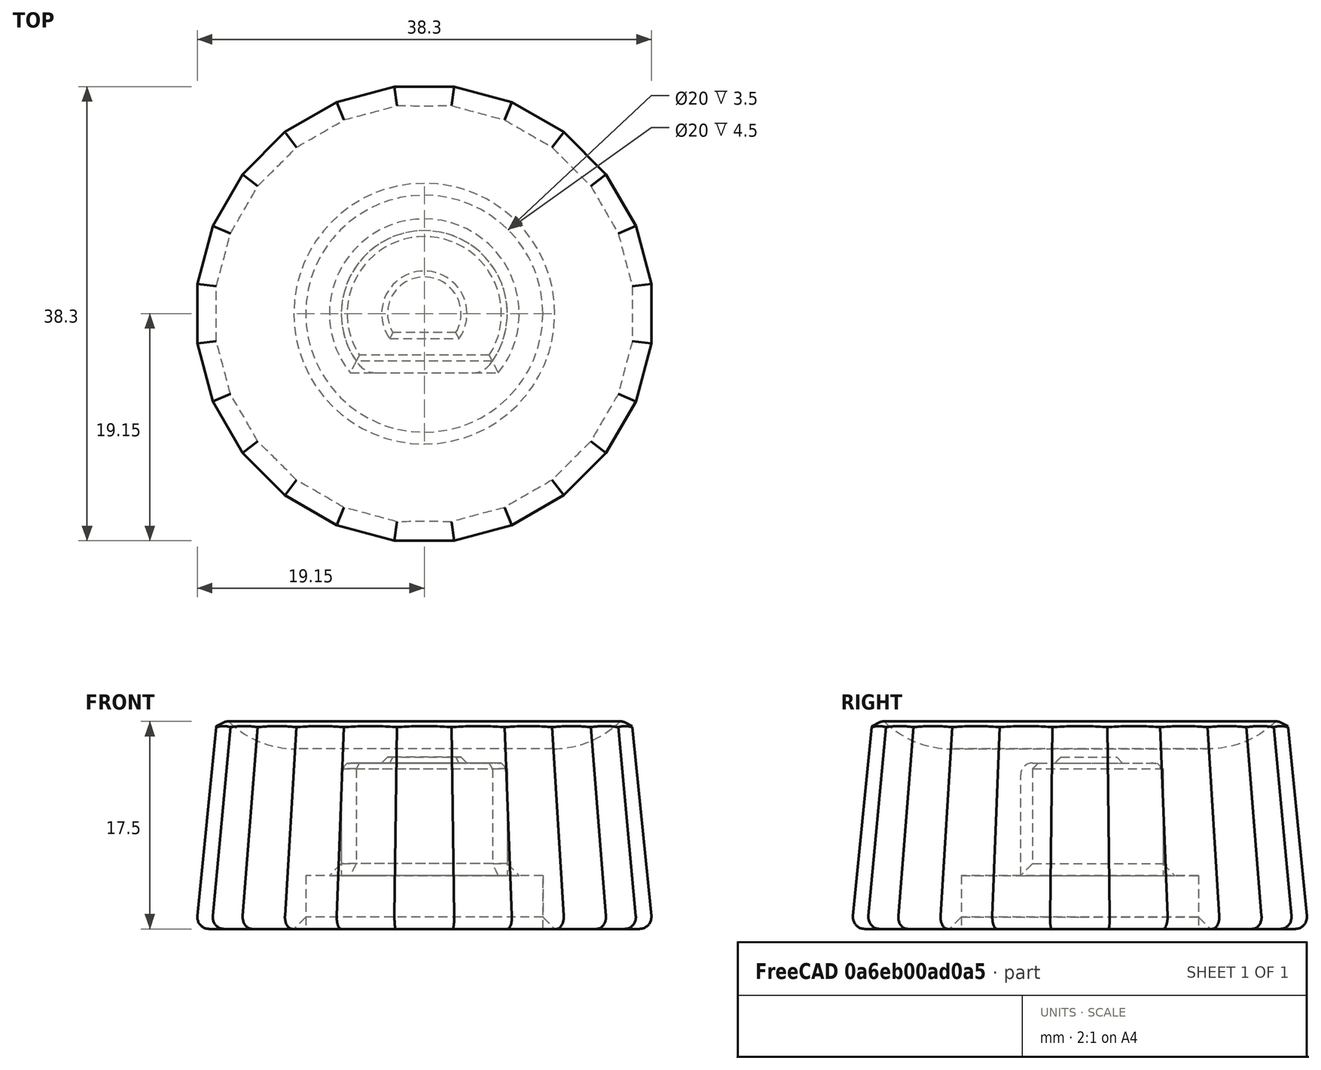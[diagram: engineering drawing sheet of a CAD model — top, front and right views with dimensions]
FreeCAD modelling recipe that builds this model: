
FCSTD DOCUMENT  (FreeCAD 1.0R39319 (Git))
Label: KNOB-TEK2
License: All rights reserved
LicenseURL: https://en.wikipedia.org/wiki/All_rights_reserved
objects: TechDraw::DrawViewDimension×14, Sketcher::SketchObject×7, TechDraw::DrawViewPart×5, TechDraw::DrawHatch×5, TechDraw::DrawViewBalloon×4, TechDraw::DrawViewAnnotation×2, PartDesign::Pocket×2, PartDesign::CoordinateSystem×2, Part::Feature×1, PartDesign::Plane×1, PartDesign::Pad×1, PartDesign::Boolean×1, TechDraw::DrawSVGTemplate×1, PartDesign::Fillet×1, PartDesign::Body×1, TechDraw::DrawComplexSection×1, TechDraw::DrawViewDimExtent×1, TechDraw::DrawPage×1
note: 58 computed .brp shape members not serialized (recipe doc carries the construction recipe); baked Part::Feature solids carry a one-line shape summary decoded from their .brp

FEATURE [Part::Feature] Part__Feature  label="alu_potmeter_002_04"
  shape: bbox 38.3 x 38.3 x 17.53 mm, 68 faces (baked)
FEATURE [PartDesign::Plane] DatumPlane
  AttachmentOffset = pos=(0,0,4.5) rot=(0,0,1;0rad)
  AttachmentSupport = -> [XY_Plane]
  Length = 60
  MapMode = 5
  Placement = pos=(0,0,4.5) rot=(0,0,1;0rad)
  ResizeMode = 0
  Width = 60
FEATURE [Sketcher::SketchObject] Sketch
  ArcFitTolerance = 0
  AttachmentSupport = -> [XY_Plane]
  FullyConstrained = true
  MakeInternals = false
  MapMode = 2
  sketch-geometry (1):
    g0: Circle CenterX=0 CenterY=0 CenterZ=0 NormalX=0 NormalY=0 NormalZ=1 AngleXU=0 Radius=15
  constraints (2):
    c: Coincident(g0,g-1)
    c: Diameter(g0) = 30
FEATURE [PartDesign::Pad] Pad
  Direction = (0,0,1)
  Length = 15
  Length2 = 10
  Profile = -> Sketch
  ReferenceAxis = -> Sketch [N_Axis]
  Refine = true
  Suppressed = false
  Type = 0
FEATURE [Sketcher::SketchObject] Sketch001
  ArcFitTolerance = 0
  AttachmentSupport = -> [DatumPlane]
  FullyConstrained = true
  MakeInternals = false
  MapMode = 5
  Placement = pos=(0,0,4.5) rot=(0,0,1;0rad)
  sketch-geometry (7):
    g0: ArcOfCircle CenterX=0 CenterY=0 CenterZ=0 NormalX=0 NormalY=0 NormalZ=1 AngleXU=0 Radius=7 StartAngle=5.63968 EndAngle=10.0683
    g1: LineSegment StartX=-4 StartY=-5 StartZ=0 EndX=4 EndY=-5 EndZ=0
    g2: Circle [constr] CenterX=0 CenterY=0 CenterZ=0 NormalX=0 NormalY=0 NormalZ=1 AngleXU=0 Radius=4.25
    g3: LineSegment [constr] StartX=0 StartY=-4.25 StartZ=0 EndX=0 EndY=-5 EndZ=0
    g4: ArcOfCircle CenterX=-4 CenterY=-3 CenterZ=0 NormalX=0 NormalY=0 NormalZ=1 AngleXU=0 Radius=2 StartAngle=3.78509 EndAngle=4.71239
    g5: ArcOfCircle CenterX=4 CenterY=-3 CenterZ=0 NormalX=0 NormalY=0 NormalZ=1 AngleXU=0 Radius=2 StartAngle=4.71239 EndAngle=5.63968
    g6: GeomPoint [constr] X=0 Y=7 Z=0
  constraints (20):
    c: Coincident(g0,g-1)
    c: Diameter(g0) = 14
    c: Horizontal(g1)
    c: Coincident(g2,g0)
    c: Diameter(g2) = 8.5
    c: PointOnObject(g3,g2)
    c: PointOnObject(g3,g1)
    c: Vertical(g3)
    c: PointOnObject(g3,g-2)
    c: DistanceY(g3,g3) = 0.75
    c: Tangent(g1,g4) = -1.5708
    c: Tangent(g0,g4) = -1.5708
    c: Tangent(g1,g5) = -1.5708
    c: Tangent(g0,g5) = -1.5708
    c: Equal(g5,g4)
    c: Diameter(g5) = 4
    c: DistanceY(g3,g0) = 5
    c: PointOnObject(g6,g0)
    c: PointOnObject(g6,g-2)
    c: DistanceY(g3,g6) = 12
FEATURE [PartDesign::Boolean] Boolean
  BaseFeature = -> Pad
  Group = -> [Part__Feature]
  Refine = true
  Suppressed = false
  Type = 0
  UsePlacement = false
FEATURE [TechDraw::DrawSVGTemplate] Template
  EditableTexts = COLOR=Sandblasted, black anodized (RAL code: 9004); CreationDate=2024/08/27; E.G.APPROVED=APPROVED; FC-Scale=2:1; FC-Title=KNOB-TEK2; IntechStudioLtd.=Intech Studio Ltd.; MATERIAL=Aluminum 6061-T6; REV=03; STANDARD=DIN 16742-TG5
  Height = 297
  Orientation = 1
  Template = <userpath>/Documents/grid-hardware/Manufacturing/FreeCAD_technical_drawing_template/A3_LandscapeTD_MODIFIED.svg
  Width = 420
FEATURE [Sketcher::SketchObject] Sketch002
  ArcFitTolerance = 0
  AttachmentSupport = -> [YZ_Plane]
  FullyConstrained = true
  MakeInternals = false
  MapMode = 5
  Placement = pos=(0,0,0) rot=(0.57735,0.57735,0.57735;2.0944rad)
  sketch-geometry (1):
    g0: LineSegment StartX=0 StartY=20 StartZ=0 EndX=0 EndY=-5 EndZ=0
  constraints (4):
    c: PointOnObject(g0,g-2)
    c: PointOnObject(g0,g-2)
    c: DistanceY(g0,g0) = 25
    c: DistanceY(g0,g-1) = 5
FEATURE [TechDraw::DrawViewAnnotation] Annotation
  Font = osifont
  LineSpace = 100
  LockPosition = false
  MaxWidth = -1
  Rotation = 0
  Scale = 2
  ScaleType = 0
  Text = Non-aesthetical side (purple): | No burrs
  TextSize = 5
  TextStyle = 0
  X = 278.355
  Y = 88.8334
FEATURE [Sketcher::SketchObject] Sketch004
  ArcFitTolerance = 0
  AttachmentSupport = -> [XY_Plane]
  FullyConstrained = true
  MakeInternals = false
  MapMode = 5
  sketch-geometry (1):
    g0: Circle CenterX=0 CenterY=0 CenterZ=0 NormalX=0 NormalY=0 NormalZ=1 AngleXU=0 Radius=10
  constraints (2):
    c: Coincident(g0,g-1)
    c: Diameter(g0) = 20
FEATURE [PartDesign::Pocket] Pocket001
  BaseFeature = -> Boolean
  Direction = (0,0,-1)
  Length = 4.5
  Length2 = 5
  Profile = -> Sketch004
  ReferenceAxis = -> Sketch004 [N_Axis]
  Refine = true
  Reversed = true
  Suppressed = false
  Type = 0
FEATURE [PartDesign::Pocket] Pocket
  BaseFeature = -> Pocket001
  Direction = (0,0,-1)
  Length = 9.5
  Length2 = 5
  Profile = -> Sketch001
  ReferenceAxis = -> Sketch001 [N_Axis]
  Refine = true
  Reversed = true
  Suppressed = false
  Type = 0
FEATURE [TechDraw::DrawViewAnnotation] Annotation001
  Font = osifont
  LineSpace = 100
  LockPosition = false
  MaxWidth = -1
  Rotation = 0
  Scale = 2
  ScaleType = 0
  Text = Section A-A
  TextSize = 4
  TextStyle = 0
  X = 199.631
  Y = 206.549
FEATURE [Sketcher::SketchObject] Sketch005
  ArcFitTolerance = 0
  AttachmentSupport = -> [DatumPlane]
  FullyConstrained = true
  MakeInternals = false
  MapMode = 5
  Placement = pos=(0,0,4.5) rot=(0,0,1;0rad)
  sketch-geometry (1):
    g0: Circle CenterX=0 CenterY=0 CenterZ=0 NormalX=0 NormalY=0 NormalZ=1 AngleXU=0 Radius=3.5
  constraints (2):
    c: Coincident(g0,g-1)
    c: Diameter(g0) = 7
FEATURE [PartDesign::Fillet] Fillet
  Base = -> Pocket [Edge136]
  BaseFeature = -> Pocket
  Radius = 1
  SupportTransform = false
  Suppressed = false
  UseAllEdges = false
FEATURE [Sketcher::SketchObject] Sketch006
  ArcFitTolerance = 0
  AttachmentSupport = -> [XY_Plane]
  FullyConstrained = true
  MakeInternals = false
  MapMode = 5
  sketch-geometry (5):
    g0: Circle CenterX=0 CenterY=0 CenterZ=0 NormalX=0 NormalY=0 NormalZ=1 AngleXU=0 Radius=6.975
    g1: Circle CenterX=0 CenterY=0 CenterZ=0 NormalX=0 NormalY=0 NormalZ=1 AngleXU=0 Radius=4.3
    g2: LineSegment StartX=-4.88876 StartY=4.975 StartZ=0 EndX=4.88876 EndY=4.975 EndZ=0
    g3: GeomPoint [constr] X=0 Y=-6.975 Z=0
    g4: GeomPoint [constr] X=0 Y=4.3 Z=0
  constraints (13):
    c: Coincident(g0,g-1)
    c: Coincident(g1,g0)
    c: PointOnObject(g2,g0)
    c: PointOnObject(g2,g0)
    c: Horizontal(g2)
    c: Diameter(g0) = 13.95
    c: Diameter(g1) = 8.6
    c: PointOnObject(g3,g0)
    c: PointOnObject(g3,g-2)
    c: DistanceY(g3,g2) = 11.95
    c: PointOnObject(g4,g1)
    c: DistanceY(g4,g2) = 0.675
    c: PointOnObject(g4,g-2)
FEATURE [Sketcher::SketchObject] Sketch007
  ArcFitTolerance = 0
  AttachmentSupport = -> [XY_Plane]
  FullyConstrained = true
  MakeInternals = false
  MapMode = 5
  sketch-geometry (4):
    g0: Circle CenterX=0 CenterY=0 CenterZ=0 NormalX=0 NormalY=0 NormalZ=1 AngleXU=0 Radius=0.1
    g1: Circle CenterX=0 CenterY=0.1 CenterZ=0 NormalX=0 NormalY=0 NormalZ=1 AngleXU=0 Radius=3.475
    g2: Circle CenterX=0 CenterY=-0.1 CenterZ=0 NormalX=0 NormalY=0 NormalZ=1 AngleXU=0 Radius=2.95
    g3: LineSegment StartX=0 StartY=-3.05 StartZ=0 EndX=0 EndY=-3.375 EndZ=0
  constraints (13):
    c: Coincident(g0,g-1)
    c: Diameter(g0) = 0.2
    c: PointOnObject(g1,g-2)
    c: PointOnObject(g1,g0)
    c: Diameter(g1) = 6.95
    c: PointOnObject(g2,g0)
    c: PointOnObject(g2,g-2)
    c: Diameter(g2) = 5.9
    c: PointOnObject(g3,g2)
    c: PointOnObject(g3,g1)
    c: Vertical(g3)
    c: PointOnObject(g3,g-2)
    c: DistanceY(g3,g3) = 0.325
FEATURE [PartDesign::CoordinateSystem] LCS_1
  AttacherType = Attacher::AttachEngine3D
  AttachmentSupport = -> [Fillet]
  MapMode = 45
  Placement = pos=(5e-16,0.740493,14) rot=(0,0,1;1.5708rad)
FEATURE [PartDesign::CoordinateSystem] LCS_2
  AttacherType = Attacher::AttachEngine3D
  AttachmentSupport = -> [Fillet]
  MapMode = 5
  Placement = pos=(0,0,14) rot=(1,0,0;3.14159rad)
FEATURE [PartDesign::Body] Body  label="KNOB-TEK2"
  AllowCompound = false
  Group = -> [DatumPlane,Sketch,Pad,Boolean,Pocket001,Sketch001,Pocket,Sketch002,Sketch004,Sketch005,Fillet,Sketch006,Sketch007,LCS_1,LCS_2]
  Origin = -> Origin
  Tip = -> Fillet
FEATURE [TechDraw::DrawViewPart] View
  CoarseView = false
  Direction = (-1,0,-3e-06)
  Focus = 100
  HardHidden = false
  IsoCount = 0
  IsoHidden = false
  IsoVisible = true
  LockPosition = false
  Perspective = false
  Rotation = 0
  Scale = 2
  ScaleType = 2
  ScrubCount = 0
  SeamHidden = false
  SeamVisible = true
  SmoothHidden = false
  SmoothVisible = true
  Source = -> [Body]
  X = 71.6241
  XDirection = (0,-1,0)
  Y = 240.603
FEATURE [TechDraw::DrawComplexSection] ComplexSection  label="Section A - A"
  BaseView = -> View
  CoarseView = false
  CutSurfaceDisplay = 3
  CuttingToolWireObject = -> Sketch002
  Direction = (0,1,-1e-16)
  FileGeomPattern = C:/Program Files/FreeCAD 0.21/data/Mod/TechDraw/PAT/FCPAT.pat
  FileHatchPattern = C:/Program Files/FreeCAD 0.21/data/Mod/TechDraw/Patterns/simple.svg
  Focus = 100
  FuseBeforeCut = false
  HardHidden = false
  HatchOffset = (0,0,0)
  HatchRotation = 0
  HatchScale = 1
  IsoCount = 0
  IsoHidden = false
  IsoVisible = true
  LockPosition = false
  NameGeomPattern = Gyémánt bevonatú
  Perspective = false
  ProjectionStrategy = 0
  Rotation = -90
  Scale = 2
  ScaleType = 0
  ScrubCount = 0
  SeamHidden = false
  SeamVisible = true
  SectionDirection = 4
  SectionLineStretch = 1
  SectionNormal = (0,1,-1e-16)
  SectionOrigin = (0,0,0)
  SectionSymbol = A
  SmoothHidden = false
  SmoothVisible = true
  Source = -> [Body]
  TrimAfterCut = false
  UsePreviousCut = false
  X = 199.631
  XDirection = (3e-06,-1e-16,-1)
  Y = 238.539
FEATURE [TechDraw::DrawViewPart] View001
  CoarseView = false
  Direction = (-3e-06,0,1)
  Focus = 100
  HardHidden = false
  IsoCount = 0
  IsoHidden = false
  IsoVisible = true
  LockPosition = false
  Perspective = false
  Rotation = 0
  Scale = 2
  ScaleType = 0
  ScrubCount = 0
  SeamHidden = false
  SeamVisible = true
  SmoothHidden = false
  SmoothVisible = true
  Source = -> [Body]
  X = 71.7073
  XDirection = (1,0,3e-06)
  Y = 150.924
FEATURE [TechDraw::DrawViewDimension] Dimension010
  AngleOverride = false
  Arbitrary = false
  ArbitraryTolerances = false
  EqualTolerance = true
  ExtensionAngle = 0
  FormatSpec = %.2w
  FormatSpecOverTolerance = %+.2w
  FormatSpecUnderTolerance = %+.2w
  Inverted = false
  LineAngle = 0
  LockPosition = false
  MeasureType = 1
  OverTolerance = 0
  References2D = -> [ComplexSection]
  Rotation = 0
  Scale = 2
  ScaleType = 0
  TheoreticalExact = false
  Type = 2
  UnderTolerance = 0
  X = 46.1971
  Y = -10.7931
FEATURE [TechDraw::DrawViewDimension] Dimension014
  AngleOverride = false
  Arbitrary = false
  ArbitraryTolerances = true
  EqualTolerance = false
  ExtensionAngle = 0
  FormatSpec = %.2w
  FormatSpecOverTolerance = +0
  FormatSpecUnderTolerance = -0.1
  Inverted = false
  LineAngle = 0
  LockPosition = false
  MeasureType = 1
  OverTolerance = 0
  References2D = -> [ComplexSection]
  Rotation = 0
  Scale = 2
  ScaleType = 0
  TheoreticalExact = false
  Type = 2
  UnderTolerance = 0
  X = 56.4159
  Y = 6.5209
FEATURE [TechDraw::DrawViewDimension] Dimension016
  AngleOverride = false
  Arbitrary = false
  ArbitraryTolerances = false
  EqualTolerance = true
  ExtensionAngle = 0
  FormatSpec = 12× %.2w
  FormatSpecOverTolerance = %+.2w
  FormatSpecUnderTolerance = %+.2w
  Inverted = false
  LineAngle = 0
  LockPosition = false
  MeasureType = 1
  OverTolerance = 0
  References2D = -> [View001]
  Rotation = 0
  Scale = 2
  ScaleType = 0
  TheoreticalExact = false
  Type = 2
  UnderTolerance = 0
  X = -56.7628
  Y = 0.276868
FEATURE [TechDraw::DrawViewPart] View002
  CoarseView = false
  Direction = (3e-06,1e-06,-1)
  Focus = 100
  HardHidden = false
  IsoCount = 0
  IsoHidden = false
  IsoVisible = true
  LockPosition = false
  Perspective = false
  Rotation = 0
  Scale = 2
  ScaleType = 0
  ScrubCount = 0
  SeamHidden = false
  SeamVisible = true
  SmoothHidden = false
  SmoothVisible = true
  Source = -> [Body]
  X = 200.492
  XDirection = (1,-3e-12,3e-06)
  Y = 152.25
FEATURE [TechDraw::DrawViewPart] View003
  CoarseView = false
  Direction = (-0.57735,0.57735,-0.57735)
  Focus = 100
  HardHidden = false
  IsoCount = 0
  IsoHidden = false
  IsoVisible = true
  LockPosition = false
  Perspective = false
  Rotation = 0
  Scale = 2
  ScaleType = 2
  ScrubCount = 0
  SeamHidden = false
  SeamVisible = true
  SmoothHidden = false
  SmoothVisible = true
  Source = -> [Body]
  X = 358.57
  XDirection = (-0.707102,-0.707111,-9.2376e-06)
  Y = 140.843
FEATURE [TechDraw::DrawViewPart] View004
  CoarseView = false
  Direction = (-0.57735,0.57735,0.57735)
  Focus = 100
  HardHidden = false
  IsoCount = 0
  IsoHidden = false
  IsoVisible = true
  LockPosition = false
  Perspective = false
  Rotation = 0
  Scale = 2
  ScaleType = 2
  ScrubCount = 0
  SeamHidden = false
  SeamVisible = true
  SmoothHidden = false
  SmoothVisible = true
  Source = -> [Body]
  X = 357.533
  XDirection = (-0.707111,-0.707101,-9.2376e-06)
  Y = 230.245
FEATURE [TechDraw::DrawHatch] Hatch  label="HatchF1"
  HatchPattern = C:/Program Files/FreeCAD 0.21/data/Mod/TechDraw/Patterns/solid.svg
  Source = -> View003 [Face1,Face44,Face15,Face7,Face3,Face19]
FEATURE [TechDraw::DrawHatch] Hatch001  label="Hatch001F13"
  HatchPattern = C:/Program Files/FreeCAD 0.21/data/Mod/TechDraw/Patterns/solid.svg
  Source = -> View004 [Face13,Face4,Face5,Face1,Face3,Face18,Face17,Face14,Face12,Face9,Face8,Face6,Face7,Face10,Face19,Face16,Face15,Face11,Face27,Face26,Face23,Face22,Face20,Face21,Face24,Face28,Face25]
FEATURE [TechDraw::DrawHatch] Hatch002  label="Hatch002F24"
  HatchPattern = C:/Program Files/FreeCAD 0.21/data/Mod/TechDraw/Patterns/solid.svg
  Source = -> View003 [Face24,Face25,Face28,Face29,Face32,Face33,Face36,Face37,Face38,Face35,Face34,Face31,Face30,Face27,Face26,Face23,Face22,Face20,Face21,Face11,Face8,Face6,Face4,Face5,Face9,Face10,Face13,Face17]
FEATURE [TechDraw::DrawViewBalloon] Balloon003
  BubbleShape = 1
  EndType = 3
  EndTypeScale = 1
  KinkLength = 0
  LockPosition = false
  OriginX = -14.9594
  OriginY = -6.7795
  Rotation = 0
  Scale = 2
  ScaleType = 0
  ShapeScale = 1
  SourceView = -> View003
  TextWrapLen = -1
  X = -29.1537
  Y = -19.8858
FEATURE [TechDraw::DrawViewDimension] Dimension027
  AngleOverride = false
  Arbitrary = false
  ArbitraryTolerances = false
  EqualTolerance = true
  ExtensionAngle = 0
  FormatSpec = ⌀%.2w
  FormatSpecOverTolerance = %+.2w
  FormatSpecUnderTolerance = %+.2w
  Inverted = false
  LineAngle = 0
  LockPosition = false
  MeasureType = 1
  OverTolerance = 0
  References2D = -> [View002]
  Rotation = 0
  Scale = 2
  ScaleType = 0
  TheoreticalExact = false
  Type = 5
  UnderTolerance = 0
  X = 58.2687
  Y = -4.50785
FEATURE [TechDraw::DrawViewDimExtent] DimExtent
  AngleOverride = false
  Arbitrary = false
  ArbitraryTolerances = false
  DirExtent = 0
  EqualTolerance = true
  ExtensionAngle = 0
  FormatSpec = ⌀%.2w
  FormatSpecOverTolerance = %+.2w
  FormatSpecUnderTolerance = %+.2w
  Inverted = false
  LineAngle = 0
  LockPosition = false
  MeasureType = 1
  OverTolerance = 0
  References2D = -> [View001]
  Rotation = 0
  Scale = 2
  ScaleType = 0
  Source = -> [View001]
  TheoreticalExact = false
  Type = 1
  UnderTolerance = 0
  X = -0.58901
  Y = -46.3131
FEATURE [TechDraw::DrawViewBalloon] Balloon
  BubbleShape = 6
  EndType = 6
  EndTypeScale = 1
  KinkLength = -0.1
  LockPosition = false
  OriginX = 19.3129
  OriginY = -26.049
  Rotation = 0
  Scale = 2
  ScaleType = 0
  ShapeScale = 1
  SourceView = -> DimExtent
  Text = A
  TextWrapLen = -1
  X = 24.4472
  Y = -26.0434
FEATURE [TechDraw::DrawViewDimension] Dimension029
  AngleOverride = false
  Arbitrary = false
  ArbitraryTolerances = false
  EqualTolerance = true
  ExtensionAngle = 0
  FormatSpec = ⌀%.2w
  FormatSpecOverTolerance = %+.2w
  FormatSpecUnderTolerance = %+.2w
  Inverted = false
  LineAngle = 0
  LockPosition = false
  MeasureType = 1
  OverTolerance = 0.05
  References2D = -> [ComplexSection]
  Rotation = 0
  Scale = 2
  ScaleType = 0
  TheoreticalExact = false
  Type = 1
  UnderTolerance = -0.05
  X = -51.7957
  Y = -20.9962
FEATURE [TechDraw::DrawViewBalloon] Balloon004
  BubbleShape = 6
  EndType = 6
  EndTypeScale = 1
  KinkLength = 0
  LockPosition = false
  OriginX = -30.2962
  OriginY = -14.1405
  Rotation = 0
  Scale = 2
  ScaleType = 0
  ShapeScale = 1
  SourceView = -> Dimension029
  Text = ◎|⌀ 0.2|A
  TextWrapLen = -1
  X = -22.8396
  Y = -16.0535
FEATURE [TechDraw::DrawViewDimension] Dimension030
  AngleOverride = false
  Arbitrary = false
  ArbitraryTolerances = false
  EqualTolerance = true
  ExtensionAngle = 0
  FormatSpec = R%.2w
  FormatSpecOverTolerance = %+.2w
  FormatSpecUnderTolerance = %+.2w
  Inverted = false
  LineAngle = 0
  LockPosition = false
  MeasureType = 1
  OverTolerance = 0
  References2D = -> [View002]
  Rotation = 0
  Scale = 2
  ScaleType = 0
  TheoreticalExact = false
  Type = 4
  UnderTolerance = 0
  X = 54.5926
  Y = 26.3888
FEATURE [TechDraw::DrawHatch] Hatch003  label="Hatch003F14"
  HatchPattern = C:/Program Files/FreeCAD 0.21/data/Mod/TechDraw/Patterns/solid.svg
  Source = -> View003 [Face14,Face16]
FEATURE [TechDraw::DrawHatch] Hatch004  label="Hatch004F18"
  HatchPattern = C:/Program Files/FreeCAD 0.21/data/Mod/TechDraw/Patterns/solid.svg
  Source = -> View003 [Face18,Face12]
FEATURE [TechDraw::DrawViewDimension] Dimension033
  AngleOverride = false
  Arbitrary = false
  ArbitraryTolerances = false
  EqualTolerance = true
  ExtensionAngle = 0
  FormatSpec = 12× %.2w
  FormatSpecOverTolerance = %+.2w
  FormatSpecUnderTolerance = %+.2w
  Inverted = false
  LineAngle = 0
  LockPosition = false
  MeasureType = 1
  OverTolerance = 0
  References2D = -> [View001]
  Rotation = 0
  Scale = 2
  ScaleType = 0
  TheoreticalExact = false
  Type = 2
  UnderTolerance = 0
  X = -46.3715
  Y = 0.067851
FEATURE [TechDraw::DrawViewDimension] Dimension038
  AngleOverride = false
  Arbitrary = false
  ArbitraryTolerances = false
  EqualTolerance = true
  ExtensionAngle = 0
  FormatSpec = %.2w
  FormatSpecOverTolerance = %+.2w
  FormatSpecUnderTolerance = %+.2w
  Inverted = false
  LineAngle = 0
  LockPosition = false
  MeasureType = 1
  OverTolerance = 0.05
  References2D = -> [View002]
  Rotation = 0
  Scale = 2
  ScaleType = 0
  TheoreticalExact = false
  Type = 2
  UnderTolerance = -0.05
  X = -63.5296
  Y = 1.33773
FEATURE [TechDraw::DrawViewDimension] Dimension039
  AngleOverride = false
  Arbitrary = false
  ArbitraryTolerances = false
  EqualTolerance = true
  ExtensionAngle = 0
  FormatSpec = R%.2w
  FormatSpecOverTolerance = %+.2w
  FormatSpecUnderTolerance = %+.2w
  Inverted = false
  LineAngle = 0
  LockPosition = false
  MeasureType = 1
  OverTolerance = 0
  References2D = -> [ComplexSection]
  Rotation = 0
  Scale = 2
  ScaleType = 0
  TheoreticalExact = false
  Type = 4
  UnderTolerance = 0
  X = -24.8071
  Y = 25.4275
FEATURE [TechDraw::DrawViewDimension] Dimension
  AngleOverride = false
  Arbitrary = false
  ArbitraryTolerances = false
  EqualTolerance = true
  ExtensionAngle = 0
  FormatSpec = R%.2w
  FormatSpecOverTolerance = %+.2w
  FormatSpecUnderTolerance = %+.2w
  Inverted = false
  LineAngle = 0
  LockPosition = false
  MeasureType = 1
  OverTolerance = 0
  References2D = -> [ComplexSection]
  Rotation = 0
  Scale = 2
  ScaleType = 0
  TheoreticalExact = false
  Type = 4
  UnderTolerance = 0
  X = -22.3763
  Y = 37.775
FEATURE [TechDraw::DrawViewDimension] Dimension040
  AngleOverride = false
  Arbitrary = false
  ArbitraryTolerances = false
  EqualTolerance = true
  ExtensionAngle = 0
  FormatSpec = %.2w
  FormatSpecOverTolerance = %+.2w
  FormatSpecUnderTolerance = %+.2w
  Inverted = false
  LineAngle = 0
  LockPosition = false
  MeasureType = 1
  OverTolerance = 0
  References2D = -> [ComplexSection]
  Rotation = 0
  Scale = 2
  ScaleType = 0
  TheoreticalExact = false
  Type = 2
  UnderTolerance = 0
  X = 50.8041
  Y = -1.3095
FEATURE [TechDraw::DrawViewDimension] Dimension041
  AngleOverride = false
  Arbitrary = false
  ArbitraryTolerances = false
  EqualTolerance = true
  ExtensionAngle = 0
  FormatSpec = %.2w
  FormatSpecOverTolerance = %+.2w
  FormatSpecUnderTolerance = %+.2w
  Inverted = false
  LineAngle = 0
  LockPosition = false
  MeasureType = 1
  OverTolerance = 0
  References2D = -> [View]
  Rotation = 0
  Scale = 2
  ScaleType = 0
  TheoreticalExact = false
  Type = 2
  UnderTolerance = 0
  X = 49.3362
  Y = 2.45968
FEATURE [TechDraw::DrawViewDimension] Dimension042
  AngleOverride = false
  Arbitrary = false
  ArbitraryTolerances = false
  EqualTolerance = true
  ExtensionAngle = 0
  FormatSpec = 12× %.2w
  FormatSpecOverTolerance = %+.2w
  FormatSpecUnderTolerance = %+.2w
  Inverted = false
  LineAngle = 0
  LockPosition = false
  MeasureType = 1
  OverTolerance = 0
  References2D = -> [View001]
  Rotation = 0
  Scale = 2
  ScaleType = 0
  TheoreticalExact = false
  Type = 2
  UnderTolerance = 0
  X = -47.1912
  Y = 0.484682
FEATURE [TechDraw::DrawViewDimension] Dimension043
  AngleOverride = false
  Arbitrary = false
  ArbitraryTolerances = false
  EqualTolerance = true
  ExtensionAngle = 0
  FormatSpec = %.2w
  FormatSpecOverTolerance = %+.2w
  FormatSpecUnderTolerance = %+.2w
  Inverted = false
  LineAngle = 0
  LockPosition = false
  MeasureType = 1
  OverTolerance = 0
  References2D = -> [View002]
  Rotation = 0
  Scale = 2
  ScaleType = 0
  TheoreticalExact = false
  Type = 2
  UnderTolerance = 0
  X = -53.6468
  Y = 6.7345
FEATURE [TechDraw::DrawViewBalloon] Balloon005
  BubbleShape = 2
  EndType = 0
  EndTypeScale = 1
  KinkLength = 5
  LockPosition = false
  OriginX = 14.2219
  OriginY = 15.3271
  Rotation = 0
  Scale = 2
  ScaleType = 0
  ShapeScale = 1
  SourceView = -> ComplexSection
  Text = 3
  TextWrapLen = -1
  X = 8.32091
  Y = 13.2809
FEATURE [TechDraw::DrawPage] Page  label="KNOB-TEK2_Drawing"
  KeepUpdated = true
  NextBalloonIndex = 10
  ProjectionType = 0
  Scale = 2
  Template = -> Template
  Views = -> [View,ComplexSection,View001,View002,Dimension010,Dimension014,Annotation,Dimension016,View003,View004,Annotation001,Balloon003,Dimension027,DimExtent,Balloon,Dimension029,Balloon004,Dimension030,Dimension033,Dimension038,Dimension039,Dimension,Dimension040,Dimension041,Dimension042,Dimension043,Balloon005]
